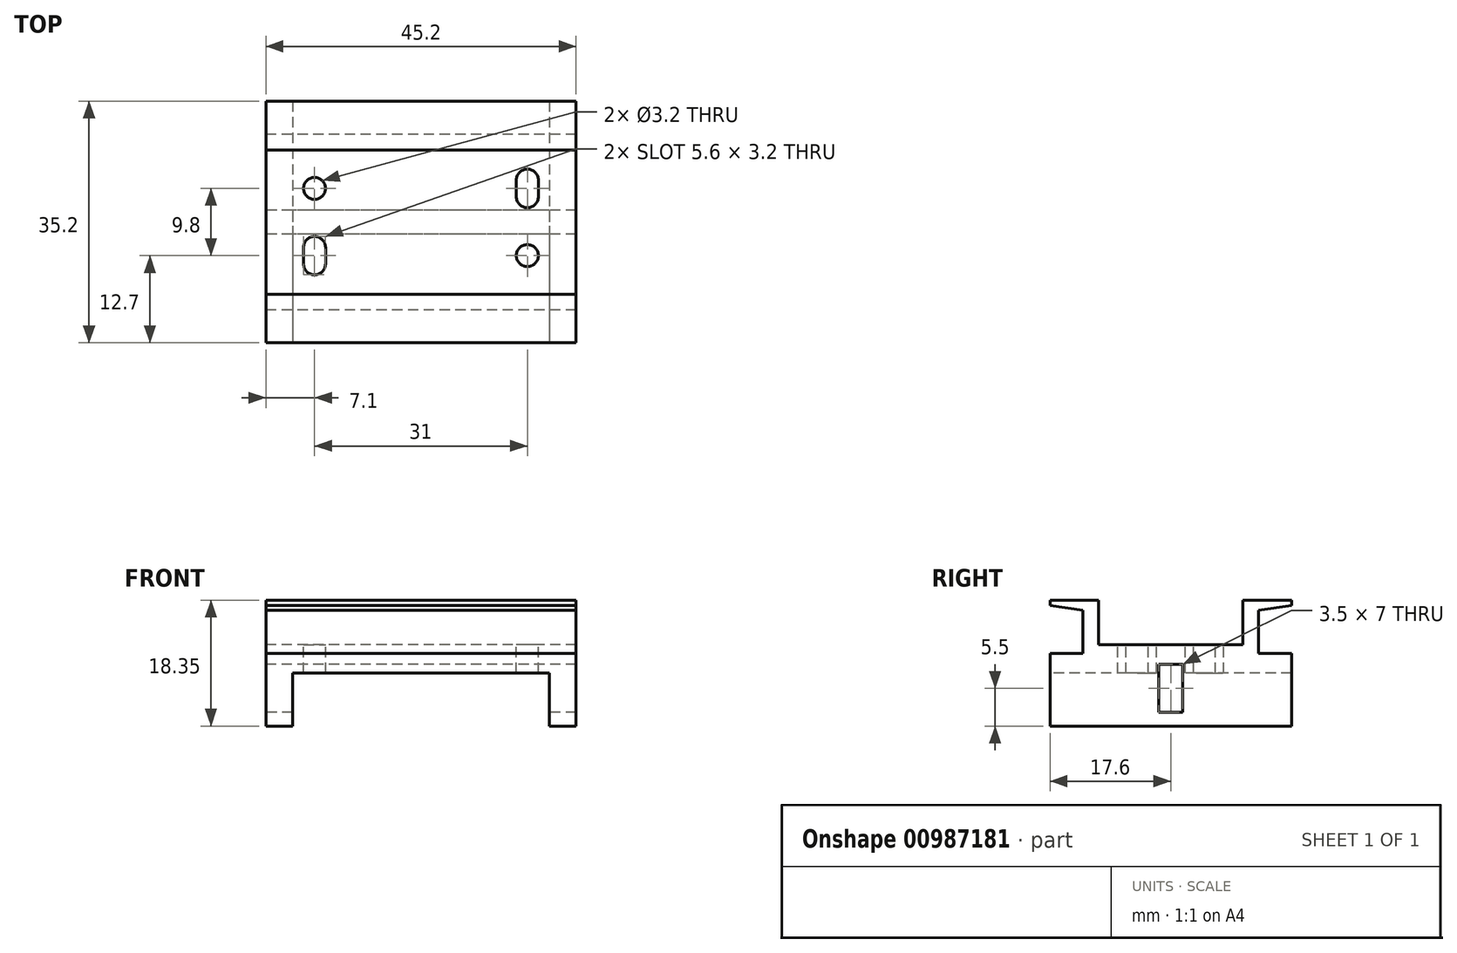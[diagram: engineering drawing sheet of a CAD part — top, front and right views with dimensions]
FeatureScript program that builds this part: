
annotation { "Feature Type Name" : "Feature", "Feature Type Description" : "" }
export const myFeature = defineFeature(function(context is Context, id is Id, definition is map)
    precondition{}
    {
        {
            var Q0;
            Q0=qCreatedBy(makeId("Top.planeOp"),FACE);
            var sketch = newSketch(context, id + "F0", { "sketchPlane" : qUnion([Q0])});
            skLineSegment(sketch, "E0.bottom", {"start": v(22.6, -17.6) * mm, "end": v(-22.6, -17.6) * mm});
            skLineSegment(sketch, "E0.top", {"start": v(22.6, 17.6) * mm, "end": v(-22.6, 17.6) * mm});
            skLineSegment(sketch, "E0.left", {"start": v(22.6, -17.6) * mm, "end": v(22.6, 17.6) * mm});
            skLineSegment(sketch, "E0.right", {"start": v(-22.6, -17.6) * mm, "end": v(-22.6, 17.6) * mm});
            skPoint(sketch, "E0.middle", {"position": v(0, 0) * mm});
            skSolve(sketch);
        }
        {
            var Q0;
            Q0 = qSketchRegion(id + "F0", true);
            extrude(context, id + "F1", {"entities" : qUnion([Q0]), "depth" : 18.35 * mm, "offsetDistance" : 25 * mm});
        }
        {
            var Q0;
            Q0=makeQuery(id+"F1.opExtrude","CAP_FACE",FACE,{"disambiguationData":[OSD([sQuery(id+"F0.wireOp",EDGE,"E0.bottom"),sQuery(id+"F0.wireOp",EDGE,"E0.top"),sQuery(id+"F0.wireOp",EDGE,"E0.left"),sQuery(id+"F0.wireOp",EDGE,"E0.right")])],"isStart":true});
            var sketch = newSketch(context, id + "F2", { "sketchPlane" : qUnion([Q0])});
            skLineSegment(sketch, "E1.bottom", {"start": v(18.7, -17.6) * mm, "end": v(-18.7, -17.6) * mm});
            skLineSegment(sketch, "E1.top", {"start": v(18.7, 17.6) * mm, "end": v(-18.7, 17.6) * mm});
            skLineSegment(sketch, "E1.left", {"start": v(18.7, -17.6) * mm, "end": v(18.7, 17.6) * mm});
            skLineSegment(sketch, "E1.right", {"start": v(-18.7, -17.6) * mm, "end": v(-18.7, 17.6) * mm});
            skPoint(sketch, "E1.middle", {"position": v(0, 0) * mm});
            skSolve(sketch);
        }
        {
            var Q0;
            Q0 = qSketchRegion(id + "F2", true);
            extrude(context, id + "F3", {"entities" : qUnion([Q0]), "operationType" : NewBodyOperationType.REMOVE, "oppositeDirection" : true, "depth" : 7.75 * mm, "offsetDistance" : 25 * mm});
        }
        {
            var Q0;
            Q0=makeQuery(id+"F1.opExtrude","CAP_FACE",FACE,{"disambiguationData":[OSD([sQuery(id+"F0.wireOp",EDGE,"E0.bottom"),sQuery(id+"F0.wireOp",EDGE,"E0.top"),sQuery(id+"F0.wireOp",EDGE,"E0.left"),sQuery(id+"F0.wireOp",EDGE,"E0.right")])],"isStart":false});
            var sketch = newSketch(context, id + "F4", { "sketchPlane" : qUnion([Q0])});
            skLineSegment(sketch, "E2.bottom", {"start": v(22.6, -10.5) * mm, "end": v(-22.6, -10.5) * mm});
            skLineSegment(sketch, "E2.top", {"start": v(22.6, 10.5) * mm, "end": v(-22.6, 10.5) * mm});
            skLineSegment(sketch, "E2.left", {"start": v(22.6, -10.5) * mm, "end": v(22.6, 10.5) * mm});
            skLineSegment(sketch, "E2.right", {"start": v(-22.6, -10.5) * mm, "end": v(-22.6, 10.5) * mm});
            skPoint(sketch, "E2.middle", {"position": v(0, 0) * mm});
            skSolve(sketch);
        }
        {
            var Q0;
            Q0 = qSketchRegion(id + "F4", true);
            extrude(context, id + "F5", {"entities" : qUnion([Q0]), "operationType" : NewBodyOperationType.REMOVE, "oppositeDirection" : true, "depth" : 6.5 * mm, "offsetDistance" : 25 * mm});
        }
        {
            var Q0;
            Q0=makeQuery(id+"F1.opExtrude","SWEPT_FACE",FACE,{"disambiguationData":[OSD([sQuery(id+"F0.wireOp",EDGE,"E0.right")])]});
            var sketch = newSketch(context, id + "F6", { "sketchPlane" : qUnion([Q0])});
            skLineSegment(sketch, "E3.bottom", {"start": v(-17.6, 10.6) * mm, "end": v(-12.8, 10.6) * mm});
            skLineSegment(sketch, "E3.top", {"start": v(-17.6, 16.85) * mm, "end": v(-12.8, 16.85) * mm});
            skLineSegment(sketch, "E3.left", {"start": v(-17.6, 10.6) * mm, "end": v(-17.6, 16.85) * mm});
            skLineSegment(sketch, "E3.right", {"start": v(-12.8, 10.6) * mm, "end": v(-12.8, 16.85) * mm});
            skLineSegment(sketch, "E4.MirrorCS", {"start": v(17.6, 16.85) * mm, "end": v(12.8, 16.85) * mm});
            skLineSegment(sketch, "E5.MirrorCS", {"start": v(17.6, 10.6) * mm, "end": v(12.8, 10.6) * mm});
            skLineSegment(sketch, "E6.MirrorCS", {"start": v(12.8, 10.6) * mm, "end": v(12.8, 16.85) * mm});
            skLineSegment(sketch, "E7.MirrorCS", {"start": v(17.6, 10.6) * mm, "end": v(17.6, 16.85) * mm});
            skSolve(sketch);
        }
        {
            var Q0;
            Q0 = qSketchRegion(id + "F6", true);
            extrude(context, id + "F7", {"entities" : qUnion([Q0]), "operationType" : NewBodyOperationType.REMOVE, "endBound" : BoundingType.THROUGH_ALL, "oppositeDirection" : true, "depth" : 25 * mm, "offsetDistance" : 25 * mm});
        }
        {
            var Q0;
            Q0=makeQuery(id+"F1.opExtrude","SWEPT_FACE",FACE,{"disambiguationData":[OSD([sQuery(id+"F0.wireOp",EDGE,"E0.right")])]});
            var sketch = newSketch(context, id + "F8", { "sketchPlane" : qUnion([Q0])});
            skLineSegment(sketch, "E8", {"start": v(-17.6, 17.6) * mm, "end": v(-12.8, 16.85) * mm});
            skLineSegment(sketch, "E9", {"start": v(17.6, 17.6) * mm, "end": v(12.8, 16.85) * mm});
            skLineSegment(sketch, "E10.bottom", {"start": v(1.75, 2) * mm, "end": v(-1.75, 2) * mm});
            skLineSegment(sketch, "E10.top", {"start": v(1.75, 9) * mm, "end": v(-1.75, 9) * mm});
            skLineSegment(sketch, "E10.left", {"start": v(1.75, 2) * mm, "end": v(1.75, 9) * mm});
            skLineSegment(sketch, "E10.right", {"start": v(-1.75, 2) * mm, "end": v(-1.75, 9) * mm});
            skPoint(sketch, "E10.middle", {"position": v(0, 5.5) * mm});
            skSolve(sketch);
        }
        {
            var Q0;
            {var subQ0=sQuery(id+"F8.wireOp",EDGE,"E8");Q0=makeQuery(id+"F8.imprint","IMPRINT",FACE,{"disambiguationData":[TD([[makeQuery(id+"F8.imprint","IMPRINT",EDGE,{"derivedFrom":subQ0}),-1.0]])]});}
            var Q1;
            {var subQ0=sQuery(id+"F8.wireOp",EDGE,"E9");Q1=makeQuery(id+"F8.imprint","IMPRINT",FACE,{"disambiguationData":[TD([[makeQuery(id+"F8.imprint","IMPRINT",EDGE,{"derivedFrom":subQ0}),1.0]])]});}
            var Q2;
            Q2=makeQuery(id+"F8.imprint","IMPRINT",FACE,{"disambiguationData":[TD([[makeQuery(id+"F8.imprint","IMPRINT",EDGE,{"derivedFrom":sQuery(id+"F8.wireOp",EDGE,"E10.bottom")}),-1.0]])]});
            extrude(context, id + "F9", {"entities" : qUnion([Q0, Q1, Q2]), "operationType" : NewBodyOperationType.REMOVE, "endBound" : BoundingType.THROUGH_ALL, "oppositeDirection" : true, "depth" : 25 * mm, "offsetDistance" : 25 * mm});
        }
        {
            var Q0;
            Q0=makeQuery(id+"F5.boolean.opBoolean","COPY",FACE,{"derivedFrom":makeQuery(id+"F5.opExtrude","CAP_FACE",FACE,{"disambiguationData":[OSD([sQuery(id+"F4.wireOp",EDGE,"E2.bottom"),sQuery(id+"F4.wireOp",EDGE,"E2.top"),sQuery(id+"F4.wireOp",EDGE,"E2.left"),sQuery(id+"F4.wireOp",EDGE,"E2.right")])],"isStart":false})});
            var sketch = newSketch(context, id + "F10", { "sketchPlane" : qUnion([Q0])});
            skCircle(sketch, "E11", {"center": v(15.5, -4.9) * mm, "radius": 1.6 * mm});
            skCircle(sketch, "E12", {"center": v(-15.5, 4.9) * mm, "radius": 1.6 * mm});
            skCircle(sketch, "E13", {"center": v(-15.5, -6.1) * mm, "radius": 1.6 * mm});
            skCircle(sketch, "E14", {"center": v(-15.5, -3.7) * mm, "radius": 1.6 * mm});
            skCircle(sketch, "E15", {"center": v(15.5, 3.7) * mm, "radius": 1.6 * mm});
            skCircle(sketch, "E16", {"center": v(15.5, 6.1) * mm, "radius": 1.6 * mm});
            skLineSegment(sketch, "E17", {"start": v(17.1, 6.1) * mm, "end": v(17.1, 3.7) * mm});
            skLineSegment(sketch, "E18", {"start": v(13.9, 3.7) * mm, "end": v(13.9, 6.1) * mm});
            skLineSegment(sketch, "E19", {"start": v(-13.9, -6.1) * mm, "end": v(-13.9, -3.7) * mm});
            skLineSegment(sketch, "E20", {"start": v(-17.1, -6.1) * mm, "end": v(-17.1, -3.7) * mm});
            skSolve(sketch);
        }
        {
            var Q0;
            Q0 = qSketchRegion(id + "F10", true);
            var Q1;
            {var subQ0=sQuery(id+"F10.wireOp",EDGE,"E16");var subQ1=sQuery(id+"F10.wireOp",EDGE,"E15");var subQ2=makeQuery(id+"F10.imprint","INTERSECT",VERTEX,{"disambiguationData":[OD(0.0)],"derivedFrom":[subQ1,subQ0]});Q1=makeQuery(id+"F10.imprint","IMPRINT",FACE,{"disambiguationData":[TD([[makeQuery(id+"F10.imprint","IMPRINT",EDGE,{"disambiguationData":[TD([[subQ2,-1.0]])],"derivedFrom":subQ1}),1.0]])]});}
            var Q2;
            {var subQ0=sQuery(id+"F10.wireOp",EDGE,"E14");var subQ1=sQuery(id+"F10.wireOp",EDGE,"E13");var subQ2=makeQuery(id+"F10.imprint","INTERSECT",VERTEX,{"disambiguationData":[OD(0.0)],"derivedFrom":[subQ1,subQ0]});Q2=makeQuery(id+"F10.imprint","IMPRINT",FACE,{"disambiguationData":[TD([[makeQuery(id+"F10.imprint","IMPRINT",EDGE,{"disambiguationData":[TD([[subQ2,-1.0]])],"derivedFrom":subQ1}),1.0]])]});}
            extrude(context, id + "F11", {"entities" : qUnion([Q0, Q1, Q2]), "operationType" : NewBodyOperationType.REMOVE, "endBound" : BoundingType.THROUGH_ALL, "oppositeDirection" : true, "depth" : 25 * mm, "offsetDistance" : 25 * mm});
        }
    });
